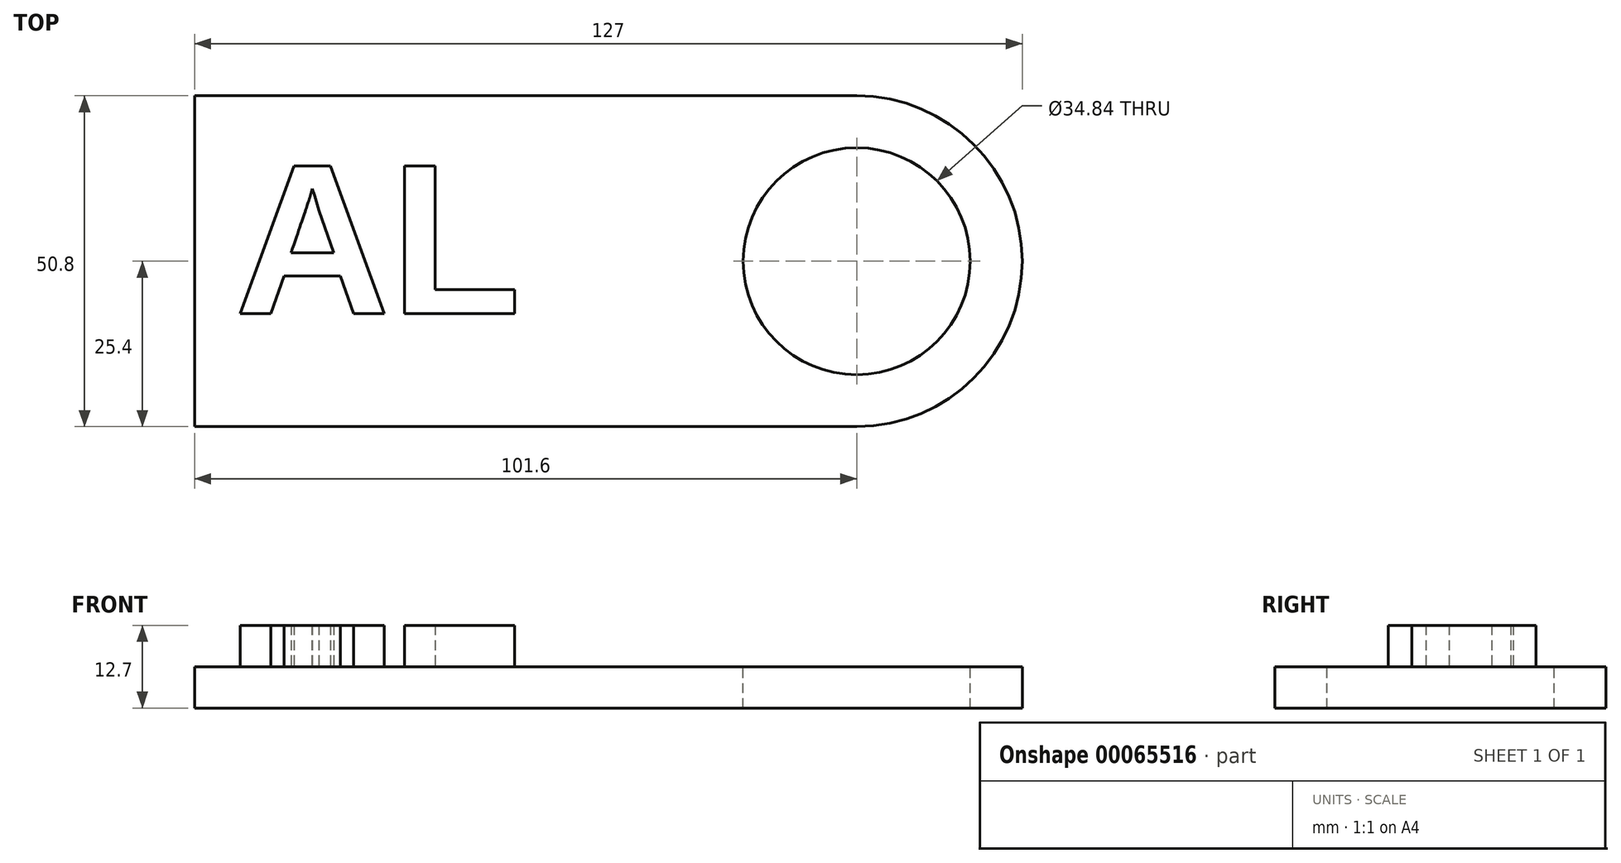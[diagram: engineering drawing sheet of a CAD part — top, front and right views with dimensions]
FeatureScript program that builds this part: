
annotation { "Feature Type Name" : "Feature", "Feature Type Description" : "" }
export const myFeature = defineFeature(function(context is Context, id is Id, definition is map)
    precondition{}
    {
        {
            var Q0;
            Q0=qCreatedBy(makeId("Top.planeOp"),FACE);
            var sketch = newSketch(context, id + "F0", { "sketchPlane" : qUnion([Q0])});
            skLineSegment(sketch, "E0.bottom", {"start": v(0, 0) * mm, "end": v(-101.6, 0) * mm});
            skLineSegment(sketch, "E0.top", {"start": v(0, 50.8) * mm, "end": v(-101.6, 50.8) * mm});
            skLineSegment(sketch, "E0.left", {"start": v(0, 0) * mm, "end": v(0, 50.8) * mm});
            skLineSegment(sketch, "E0.right", {"start": v(-101.6, 0) * mm, "end": v(-101.6, 50.8) * mm});
            skSolve(sketch);
        }
        {
            var Q0;
            Q0=makeQuery(id+"F0.imprint","IMPRINT",FACE,{"disambiguationData":[TD([[makeQuery(id+"F0.imprint","IMPRINT",EDGE,{"derivedFrom":sQuery(id+"F0.wireOp",EDGE,"E0.bottom")}),-1.0]])]});
            extrude(context, id + "F1", {"entities" : qUnion([Q0]), "depth" : 6.35 * mm});
        }
        {
            var Q0;
            Q0=makeQuery(id+"F1.opExtrude","CAP_FACE",FACE,{"disambiguationData":[OSD([sQuery(id+"F0.wireOp",EDGE,"E0.bottom"),sQuery(id+"F0.wireOp",EDGE,"E0.top"),sQuery(id+"F0.wireOp",EDGE,"E0.left"),sQuery(id+"F0.wireOp",EDGE,"E0.right")])],"isStart":false});
            var sketch = newSketch(context, id + "F2", { "sketchPlane" : qUnion([Q0])});
            skArc(sketch, "E1", {"start": v(0, 0) * mm, "mid": v(25.4, 25.4) * mm, "end": v(0, 50.8) * mm});
            skLineSegment(sketch, "E2", {"start": v(0, 50.8) * mm, "end": v(0, 0) * mm});
            skSolve(sketch);
        }
        {
            var Q0;
            Q0=makeQuery(id+"F2.imprint","IMPRINT",FACE,{"disambiguationData":[TD([[makeQuery(id+"F2.imprint","IMPRINT",EDGE,{"derivedFrom":sQuery(id+"F2.wireOp",EDGE,"E1")}),1.0]])]});
            var Q1;
            Q1=qCreatedBy(makeId("Front.planeOp"),FACE);
            extrude(context, id + "F3", {"entities" : qUnion([Q0]), "operationType" : NewBodyOperationType.ADD, "oppositeDirection" : true, "endBoundEntityFace" : qUnion([Q1]), "depth" : 6.35 * mm});
        }
        {
            var Q0;
            Q0=makeQuery(id+"F3.boolean.opBoolean","MERGE",FACE,{"derivedFrom":[makeQuery(id+"F1.opExtrude","CAP_FACE",FACE,{"disambiguationData":[OSD([sQuery(id+"F0.wireOp",EDGE,"E0.bottom"),sQuery(id+"F0.wireOp",EDGE,"E0.top"),sQuery(id+"F0.wireOp",EDGE,"E0.left"),sQuery(id+"F0.wireOp",EDGE,"E0.right")])],"isStart":false}),makeQuery(id+"F3.opExtrude","CAP_FACE",FACE,{"disambiguationData":[OSD([sQuery(id+"F2.wireOp",EDGE,"E1"),sQuery(id+"F2.wireOp",EDGE,"E2")])],"isStart":true})]});
            var sketch = newSketch(context, id + "F4", { "sketchPlane" : qUnion([Q0])});
            skCircle(sketch, "E3", {"center": v(0, 25.4) * mm, "radius": 17.42 * mm});
            skSolve(sketch);
        }
        {
            var Q0;
            Q0 = qSketchRegion(id + "F4", true);
            extrude(context, id + "F5", {"entities" : qUnion([Q0]), "operationType" : NewBodyOperationType.REMOVE, "endBound" : BoundingType.THROUGH_ALL, "oppositeDirection" : true, "depth" : 25.4 * mm});
        }
        {
            var Q0;
            Q0=makeQuery(id+"F3.boolean.opBoolean","MERGE",FACE,{"derivedFrom":[makeQuery(id+"F1.opExtrude","CAP_FACE",FACE,{"disambiguationData":[OSD([sQuery(id+"F0.wireOp",EDGE,"E0.bottom"),sQuery(id+"F0.wireOp",EDGE,"E0.top"),sQuery(id+"F0.wireOp",EDGE,"E0.left"),sQuery(id+"F0.wireOp",EDGE,"E0.right")])],"isStart":false}),makeQuery(id+"F3.opExtrude","CAP_FACE",FACE,{"disambiguationData":[OSD([sQuery(id+"F2.wireOp",EDGE,"E1"),sQuery(id+"F2.wireOp",EDGE,"E2")])],"isStart":true})]});
            var sketch = newSketch(context, id + "F6", { "sketchPlane" : qUnion([Q0])});
            skText(sketch, "E4", { "text": "AL", "fontName": "Arimo-Bold.ttf"});
            const initialGuessF6  = {"E4": [-0.09543, 0.01735, 1, 0, 0.02375]};
            skSetInitialGuess(sketch, initialGuessF6);
            skSolve(sketch);
        }
        {
            var Q0;
            Q0 = qSketchRegion(id + "F6", true);
            extrude(context, id + "F7", {"entities" : qUnion([Q0]), "operationType" : NewBodyOperationType.ADD, "depth" : 6.35 * mm});
        }
    });
